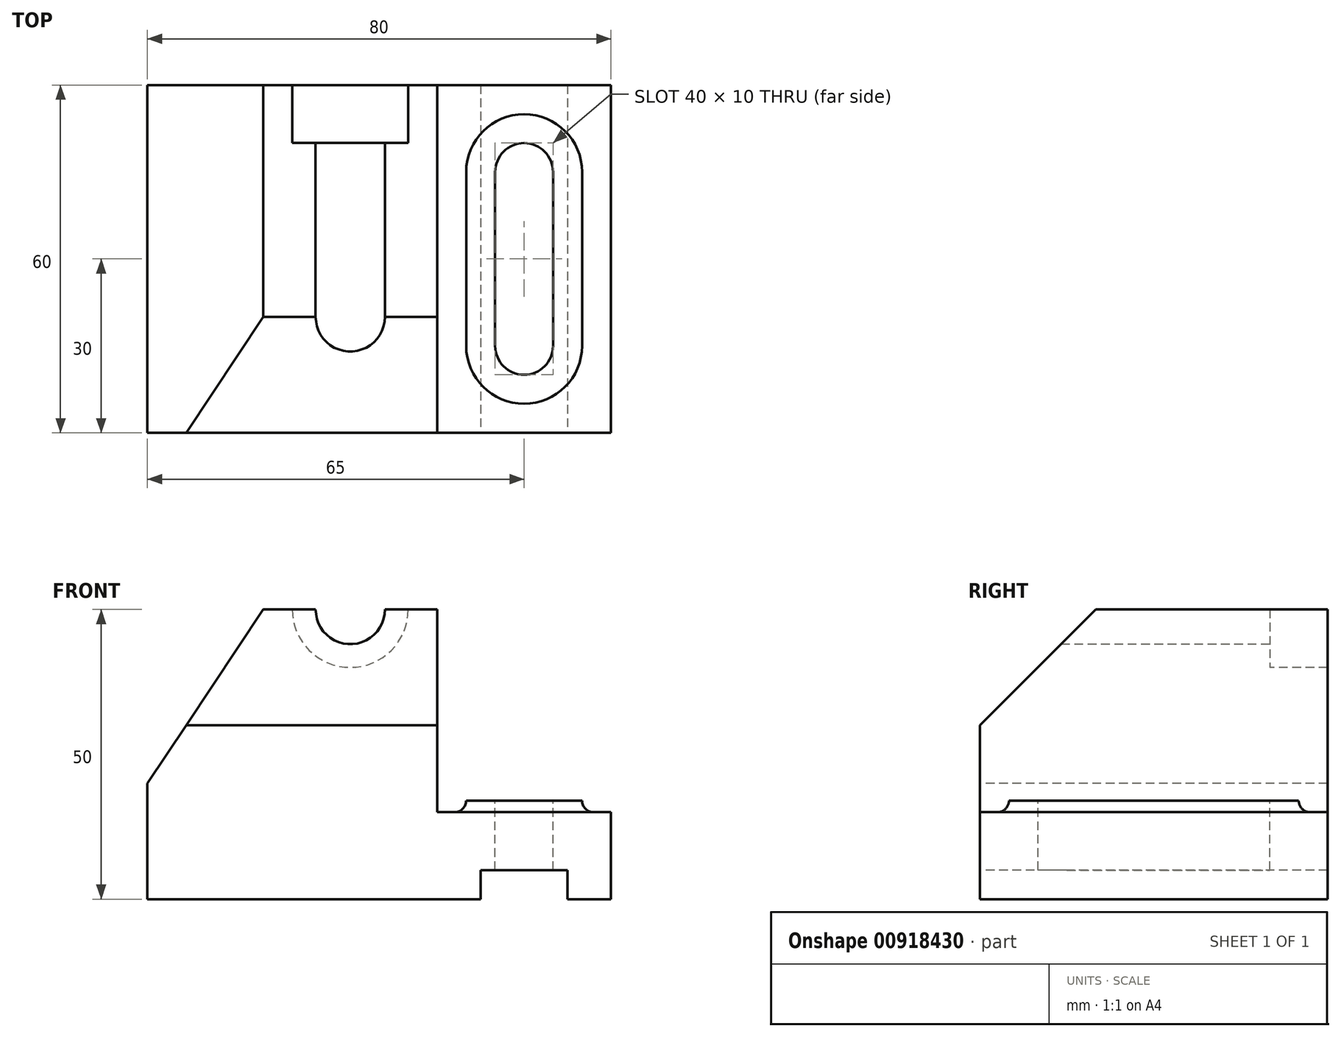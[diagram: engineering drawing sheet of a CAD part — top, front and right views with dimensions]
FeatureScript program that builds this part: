
annotation { "Feature Type Name" : "Feature", "Feature Type Description" : "" }
export const myFeature = defineFeature(function(context is Context, id is Id, definition is map)
    precondition{}
    {
        {
            var Q0;
            Q0=qCreatedBy(makeId("Top.planeOp"),FACE);
            var sketch = newSketch(context, id + "F0", { "sketchPlane" : qUnion([Q0])});
            skLineSegment(sketch, "E0.bottom", {"start": v(40, -30) * mm, "end": v(-40, -30) * mm});
            skLineSegment(sketch, "E0.top", {"start": v(40, 30) * mm, "end": v(-40, 30) * mm});
            skLineSegment(sketch, "E0.left", {"start": v(40, -30) * mm, "end": v(40, 30) * mm});
            skLineSegment(sketch, "E0.right", {"start": v(-40, -30) * mm, "end": v(-40, 30) * mm});
            skPoint(sketch, "E0.middle", {"position": v(0, 0) * mm});
            skSolve(sketch);
        }
        {
            var Q0;
            Q0=makeQuery(id+"F0.imprint","IMPRINT",FACE,{"disambiguationData":[TD([[makeQuery(id+"F0.imprint","IMPRINT",EDGE,{"derivedFrom":sQuery(id+"F0.wireOp",EDGE,"E0.bottom")}),-1.0]])]});
            extrude(context, id + "F1", {"entities" : qUnion([Q0]), "depth" : 50 * mm, "offsetDistance" : 25 * mm});
        }
        {
            var Q0;
            Q0=makeQuery(id+"F1.opExtrude","SWEPT_FACE",FACE,{"disambiguationData":[OSD([sQuery(id+"F0.wireOp",EDGE,"E0.bottom")])]});
            var sketch = newSketch(context, id + "F2", { "sketchPlane" : qUnion([Q0])});
            skLineSegment(sketch, "E1.bottom", {"start": v(40, 50) * mm, "end": v(10, 50) * mm});
            skLineSegment(sketch, "E1.top", {"start": v(40, 17) * mm, "end": v(10, 17) * mm});
            skLineSegment(sketch, "E1.left", {"start": v(40, 50) * mm, "end": v(40, 17) * mm});
            skLineSegment(sketch, "E1.right", {"start": v(10, 50) * mm, "end": v(10, 17) * mm});
            skSolve(sketch);
        }
        {
            var Q0;
            Q0=makeQuery(id+"F2.imprint","IMPRINT",FACE,{"disambiguationData":[TD([[makeQuery(id+"F2.imprint","IMPRINT",EDGE,{"derivedFrom":sQuery(id+"F2.wireOp",EDGE,"E1.bottom")}),1.0]])]});
            extrude(context, id + "F3", {"entities" : qUnion([Q0]), "operationType" : NewBodyOperationType.REMOVE, "endBound" : BoundingType.THROUGH_ALL, "oppositeDirection" : true, "depth" : 25 * mm, "offsetDistance" : 25 * mm});
        }
        {
            var Q0;
            Q0=makeQuery(id+"F3.boolean.opBoolean","COPY",FACE,{"derivedFrom":makeQuery(id+"F3.opExtrude","SWEPT_FACE",FACE,{"disambiguationData":[OSD([sQuery(id+"F2.wireOp",EDGE,"E1.top")])]})});
            var sketch = newSketch(context, id + "F4", { "sketchPlane" : qUnion([Q0])});
            skLineSegment(sketch, "E2", {"start": v(-56.8, 0) * mm, "end": v(63.1, 0) * mm, "construction": true});
            skLineSegment(sketch, "E3.0", {"start": v(25, -30) * mm, "end": v(25, 30) * mm, "construction": true});
            skLineSegment(sketch, "E4.0", {"start": v(40, -15) * mm, "end": v(10, -15) * mm, "construction": true});
            skLineSegment(sketch, "E5.0", {"start": v(40, 15) * mm, "end": v(10, 15) * mm, "construction": true});
            skLineSegment(sketch, "E6.0", {"start": v(30, -15) * mm, "end": v(30, 15) * mm});
            skLineSegment(sketch, "E7.0", {"start": v(20, -15) * mm, "end": v(20, 15) * mm});
            skArc(sketch, "E8", {"start": v(30, 15) * mm, "mid": v(25, 20) * mm, "end": v(20, 15) * mm});
            skArc(sketch, "E9.MirrorCS", {"start": v(30, -15) * mm, "mid": v(25, -20) * mm, "end": v(20, -15) * mm});
            skSolve(sketch);
        }
        {
            var Q0;
            Q0=makeQuery(id+"F4.imprint","IMPRINT",FACE,{"disambiguationData":[TD([[makeQuery(id+"F4.imprint","IMPRINT",EDGE,{"derivedFrom":sQuery(id+"F4.wireOp",EDGE,"E6.0")}),1.0]])]});
            extrude(context, id + "F5", {"entities" : qUnion([Q0]), "operationType" : NewBodyOperationType.REMOVE, "endBound" : BoundingType.THROUGH_ALL, "oppositeDirection" : true, "depth" : 25 * mm, "offsetDistance" : 25 * mm});
        }
        {
            var Q0;
            Q0=makeQuery(id+"F3.boolean.opBoolean","COPY",FACE,{"derivedFrom":makeQuery(id+"F3.opExtrude","SWEPT_FACE",FACE,{"disambiguationData":[OSD([sQuery(id+"F2.wireOp",EDGE,"E1.top")])]})});
            var sketch = newSketch(context, id + "F6", { "sketchPlane" : qUnion([Q0])});
            skLineSegment(sketch, "E10.bottom", {"start": v(10, 30) * mm, "end": v(40, 30) * mm});
            skLineSegment(sketch, "E10.top", {"start": v(10, -30) * mm, "end": v(40, -30) * mm});
            skLineSegment(sketch, "E10.left", {"start": v(10, 30) * mm, "end": v(10, -30) * mm});
            skLineSegment(sketch, "E10.right", {"start": v(40, 30) * mm, "end": v(40, -30) * mm});
            skLineSegment(sketch, "E11.0", {"start": v(35, -15) * mm, "end": v(35, 15) * mm});
            skArc(sketch, "E12.0", {"start": v(35, 15) * mm, "mid": v(25, 25) * mm, "end": v(15, 15) * mm});
            skLineSegment(sketch, "E13.0", {"start": v(15, -15) * mm, "end": v(15, 15) * mm});
            skArc(sketch, "E14.0", {"start": v(35, -15) * mm, "mid": v(25, -25) * mm, "end": v(15, -15) * mm});
            skSolve(sketch);
        }
        {
            var Q0;
            Q0=makeQuery(id+"F6.imprint","IMPRINT",FACE,{"disambiguationData":[TD([[makeQuery(id+"F6.imprint","IMPRINT",EDGE,{"derivedFrom":sQuery(id+"F6.wireOp",EDGE,"E10.bottom")}),1.0]])]});
            extrude(context, id + "F7", {"entities" : qUnion([Q0]), "operationType" : NewBodyOperationType.REMOVE, "oppositeDirection" : true, "depth" : 2 * mm, "offsetDistance" : 25 * mm});
        }
        {
            var Q0;
            Q0=makeQuery(id+"F1.opExtrude","SWEPT_FACE",FACE,{"disambiguationData":[OSD([sQuery(id+"F0.wireOp",EDGE,"E0.bottom")])]});
            var sketch = newSketch(context, id + "F8", { "sketchPlane" : qUnion([Q0])});
            skLineSegment(sketch, "E15.0", {"start": v(25, 50) * mm, "end": v(25, 0) * mm, "construction": true});
            skLineSegment(sketch, "E16.bottom", {"start": v(17.5, 5) * mm, "end": v(32.5, 5) * mm});
            skLineSegment(sketch, "E16.top", {"start": v(17.5, 0) * mm, "end": v(32.5, 0) * mm});
            skLineSegment(sketch, "E16.left", {"start": v(17.5, 5) * mm, "end": v(17.5, 0) * mm});
            skLineSegment(sketch, "E16.right", {"start": v(32.5, 5) * mm, "end": v(32.5, 0) * mm});
            skSolve(sketch);
        }
        {
            var Q0;
            Q0=makeQuery(id+"F8.imprint","IMPRINT",FACE,{"disambiguationData":[TD([[makeQuery(id+"F8.imprint","IMPRINT",EDGE,{"derivedFrom":sQuery(id+"F8.wireOp",EDGE,"E16.bottom")}),-1.0]])]});
            extrude(context, id + "F9", {"entities" : qUnion([Q0]), "operationType" : NewBodyOperationType.REMOVE, "endBound" : BoundingType.THROUGH_ALL, "oppositeDirection" : true, "depth" : 25 * mm, "offsetDistance" : 25 * mm});
        }
        {
            var Q0;
            Q0=makeQuery(id+"F7.boolean.opBoolean","COPY",EDGE,{"derivedFrom":makeQuery(id+"F7.opExtrude","CAP_EDGE",EDGE,{"disambiguationData":[OSD([sQuery(id+"F6.wireOp",EDGE,"E11.0")])],"isStart":false})});
            fillet(context, id + "F10", {"entities" : qUnion([Q0]), "radius" : 2 * mm, "tangentPropagation" : true, "allowEdgeOverflow" : false});
        }
        {
            var Q0;
            Q0=makeQuery(id+"F1.opExtrude","SWEPT_FACE",FACE,{"disambiguationData":[OSD([sQuery(id+"F0.wireOp",EDGE,"E0.bottom")])]});
            var sketch = newSketch(context, id + "F11", { "sketchPlane" : qUnion([Q0])});
            skLineSegment(sketch, "E17", {"start": v(-20, 50) * mm, "end": v(-40, 20) * mm});
            skLineSegment(sketch, "E18", {"start": v(-40, 20) * mm, "end": v(-40, 50) * mm});
            skLineSegment(sketch, "E19", {"start": v(-40, 50) * mm, "end": v(-20, 50) * mm});
            skSolve(sketch);
        }
        {
            var Q0;
            Q0=makeQuery(id+"F11.imprint","IMPRINT",FACE,{"disambiguationData":[TD([[makeQuery(id+"F11.imprint","IMPRINT",EDGE,{"derivedFrom":sQuery(id+"F11.wireOp",EDGE,"E17")}),-1.0]])]});
            extrude(context, id + "F12", {"entities" : qUnion([Q0]), "operationType" : NewBodyOperationType.REMOVE, "endBound" : BoundingType.THROUGH_ALL, "oppositeDirection" : true, "depth" : 25 * mm, "offsetDistance" : 25 * mm});
        }
        {
            var Q0;
            Q0=makeQuery(id+"F1.opExtrude","CAP_FACE",FACE,{"disambiguationData":[OSD([sQuery(id+"F0.wireOp",EDGE,"E0.bottom"),sQuery(id+"F0.wireOp",EDGE,"E0.top"),sQuery(id+"F0.wireOp",EDGE,"E0.left"),sQuery(id+"F0.wireOp",EDGE,"E0.right")])],"isStart":false});
            var sketch = newSketch(context, id + "F13", { "sketchPlane" : qUnion([Q0])});
            skLineSegment(sketch, "E20", {"start": v(-5, 47.99) * mm, "end": v(-5, -51.2) * mm, "construction": true});
            skLineSegment(sketch, "E21.bottom", {"start": v(-11, 30) * mm, "end": v(-5, 30) * mm});
            skLineSegment(sketch, "E21.top", {"start": v(-11, -18.93) * mm, "end": v(-5, -18.93) * mm});
            skLineSegment(sketch, "E21.left", {"start": v(-11, 30) * mm, "end": v(-11, -18.93) * mm});
            skLineSegment(sketch, "E21.right", {"start": v(-5, 30) * mm, "end": v(-5, -18.93) * mm});
            skSolve(sketch);
        }
        {
            var Q0;
            {var subQ0=sQuery(id+"F13.wireOp",EDGE,"E21.bottom");Q0=makeQuery(id+"F13.imprint","IMPRINT",FACE,{"disambiguationData":[TD([[makeQuery(id+"F13.imprint","IMPRINT",EDGE,{"derivedFrom":subQ0}),1.0]])]});}
            var Q1;
            Q1=sQuery(id+"F13.wireOp",EDGE,"E20");
            revolve(context, id + "F14", {"operationType" : NewBodyOperationType.REMOVE, "surfaceOperationType" : NewSurfaceOperationType.NEW, "entities" : qUnion([Q0]), "axis" : qUnion([Q1]), "revolveType" : RevolveType.FULL, "oppositeDirection" : true});
        }
        {
            var Q0;
            Q0=makeQuery(id+"F17.opChamfer","SPLIT",FACE,{"disambiguationData":[OD(1.0)],"derivedFrom":makeQuery(id+"F1.opExtrude","CAP_FACE",FACE,{"disambiguationData":[OSD([sQuery(id+"F0.wireOp",EDGE,"E0.bottom"),sQuery(id+"F0.wireOp",EDGE,"E0.top"),sQuery(id+"F0.wireOp",EDGE,"E0.left"),sQuery(id+"F0.wireOp",EDGE,"E0.right")])],"isStart":false})});
            var sketch = newSketch(context, id + "F15", { "sketchPlane" : qUnion([Q0])});
            skLineSegment(sketch, "E22.bottom", {"start": v(-15, 30) * mm, "end": v(-5, 30) * mm});
            skLineSegment(sketch, "E22.top", {"start": v(-15, 20) * mm, "end": v(-5, 20) * mm});
            skLineSegment(sketch, "E22.left", {"start": v(-15, 30) * mm, "end": v(-15, 20) * mm});
            skLineSegment(sketch, "E22.right", {"start": v(-5, 30) * mm, "end": v(-5, 20) * mm});
            skSolve(sketch);
        }
        {
            var Q0;
            {var subQ6=sQuery(id+"F15.wireOp",EDGE,"E22.left");Q0=makeQuery(id+"F15.imprint","IMPRINT",FACE,{"disambiguationData":[TD([[makeQuery(id+"F15.imprint","IMPRINT",EDGE,{"derivedFrom":subQ6}),1.0]])]});}
            var Q1;
            Q1=sQuery(id+"F15.wireOp",EDGE,"E22.right");
            revolve(context, id + "F16", {"operationType" : NewBodyOperationType.REMOVE, "surfaceOperationType" : NewSurfaceOperationType.NEW, "entities" : qUnion([Q0]), "axis" : qUnion([Q1]), "revolveType" : RevolveType.FULL, "oppositeDirection" : true});
        }
        {
            var Q0;
            Q0=makeQuery(id+"F1.opExtrude","CAP_EDGE",EDGE,{"disambiguationData":[OSD([sQuery(id+"F0.wireOp",EDGE,"E0.bottom")])],"isStart":false});
            chamfer(context, id + "F17", {"entities" : qUnion([Q0]), "width" : 20 * mm, "tangentPropagation" : true});
        }
    });
